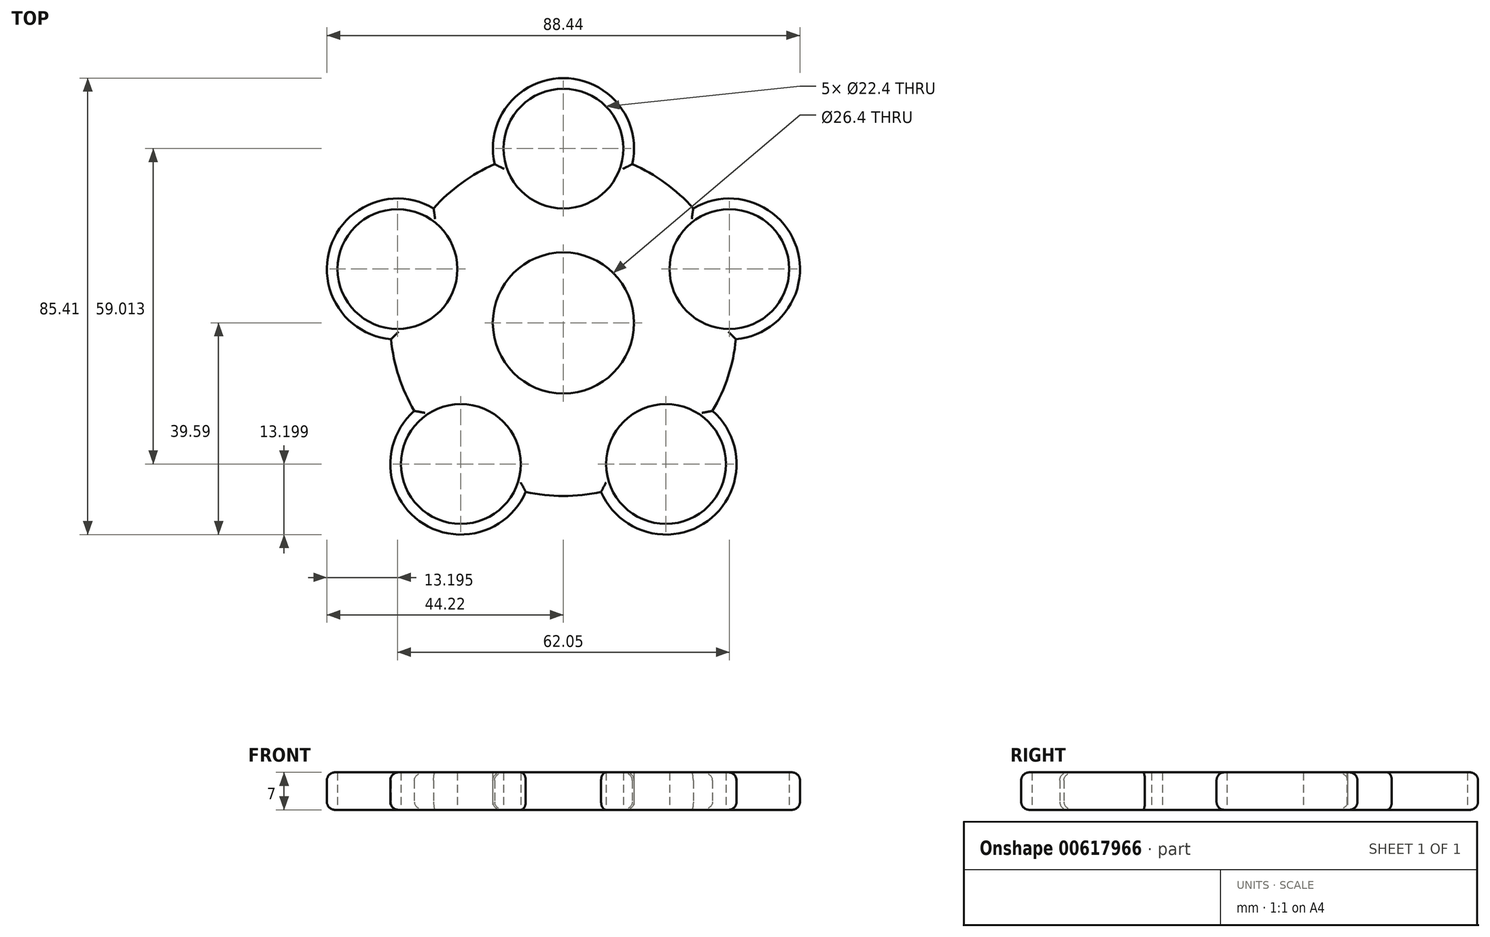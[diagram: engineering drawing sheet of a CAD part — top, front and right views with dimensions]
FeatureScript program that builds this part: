
annotation { "Feature Type Name" : "Feature", "Feature Type Description" : "" }
export const myFeature = defineFeature(function(context is Context, id is Id, definition is map)
    precondition{}
    {
        {
            var Q0;
            Q0=qCreatedBy(makeId("Top.planeOp"),FACE);
            var sketch = newSketch(context, id + "F0", { "sketchPlane" : qUnion([Q0])});
            skCircle(sketch, "E0", {"center": v(0, 0) * mm, "radius": 11.2 * mm});
            skCircle(sketch, "E1", {"center": v(0, 0) * mm, "radius": 13.2 * mm});
            skCircle(sketch, "E2", {"center": v(0, 32.62) * mm, "radius": 11.2 * mm});
            skCircle(sketch, "E3", {"center": v(0, 32.62) * mm, "radius": 13.2 * mm});
            skArc(sketch, "E4.1.0", {"start": v(-24.27, 21.42) * mm, "mid": v(-43.58, 14.16) * mm, "end": v(-32.23, -3.06) * mm});
            skCircle(sketch, "E4.1.1", {"center": v(-31.02, 10.08) * mm, "radius": 11.2 * mm});
            skArc(sketch, "E4.2.0", {"start": v(-27.88, -16.47) * mm, "mid": v(-26.93, -37.07) * mm, "end": v(-7.05, -31.6) * mm});
            skCircle(sketch, "E4.2.1", {"center": v(-19.17, -26.4) * mm, "radius": 11.2 * mm});
            skArc(sketch, "E4.3.0", {"start": v(7.05, -31.6) * mm, "mid": v(26.93, -37.07) * mm, "end": v(27.88, -16.47) * mm});
            skCircle(sketch, "E4.3.1", {"center": v(19.17, -26.4) * mm, "radius": 11.2 * mm});
            skArc(sketch, "E5.1.4.0", {"start": v(32.23, -3.06) * mm, "mid": v(43.58, 14.16) * mm, "end": v(24.27, 21.42) * mm});
            skCircle(sketch, "E5.2.4.0", {"center": v(31.02, 10.08) * mm, "radius": 11.2 * mm});
            skArc(sketch, "E6", {"start": v(25.57, 19.86) * mm, "mid": v(19.03, 26.2) * mm, "end": v(10.99, 30.45) * mm});
            skArc(sketch, "E7.trimOffspring", {"start": v(26.79, -18.18) * mm, "mid": v(30.8, -10) * mm, "end": v(32.36, -1.04) * mm});
            skArc(sketch, "E8.trimOffspring", {"start": v(-9.01, -31.1) * mm, "mid": v(0, -32.38) * mm, "end": v(9.01, -31.1) * mm});
            skArc(sketch, "E9.trimOffspring", {"start": v(-32.36, -1.04) * mm, "mid": v(-30.8, -10) * mm, "end": v(-26.79, -18.18) * mm});
            skArc(sketch, "E10.trimOffspring", {"start": v(-10.99, 30.45) * mm, "mid": v(-19.03, 26.2) * mm, "end": v(-25.57, 19.86) * mm});
            skSolve(sketch);
        }
        {
            var Q0;
            Q0=makeQuery(id+"F0.imprint","IMPRINT",FACE,{"disambiguationData":[TD([[makeQuery(id+"F0.imprint","IMPRINT",EDGE,{"derivedFrom":sQuery(id+"F0.wireOp",EDGE,"E1")}),-1.0]])]});
            var Q1;
            {var subQ0=sQuery(id+"F0.wireOp",EDGE,"E6");var subQ1=sQuery(id+"F0.wireOp",EDGE,"E2");var subQ2=makeQuery(id+"F0.imprint","INTERSECT",VERTEX,{"derivedFrom":[subQ1,subQ0]});Q1=makeQuery(id+"F0.imprint","IMPRINT",FACE,{"disambiguationData":[TD([[makeQuery(id+"F0.imprint","IMPRINT",EDGE,{"disambiguationData":[TD([[subQ2,-1.0]])],"derivedFrom":subQ1}),-1.0]])]});}
            var Q2;
            {var subQ0=sQuery(id+"F0.wireOp",EDGE,"E5.1.4.0");Q2=makeQuery(id+"F0.imprint","IMPRINT",FACE,{"disambiguationData":[TD([[makeQuery(id+"F0.imprint","IMPRINT",EDGE,{"derivedFrom":subQ0}),1.0]])]});}
            var Q3;
            {var subQ0=sQuery(id+"F0.wireOp",EDGE,"E4.3.0");Q3=makeQuery(id+"F0.imprint","IMPRINT",FACE,{"disambiguationData":[TD([[makeQuery(id+"F0.imprint","IMPRINT",EDGE,{"derivedFrom":subQ0}),1.0]])]});}
            var Q4;
            {var subQ0=sQuery(id+"F0.wireOp",EDGE,"E4.2.0");Q4=makeQuery(id+"F0.imprint","IMPRINT",FACE,{"disambiguationData":[TD([[makeQuery(id+"F0.imprint","IMPRINT",EDGE,{"derivedFrom":subQ0}),1.0]])]});}
            var Q5;
            {var subQ0=sQuery(id+"F0.wireOp",EDGE,"E4.1.0");Q5=makeQuery(id+"F0.imprint","IMPRINT",FACE,{"disambiguationData":[TD([[makeQuery(id+"F0.imprint","IMPRINT",EDGE,{"derivedFrom":subQ0}),1.0]])]});}
            var Q6;
            {var subQ0=sQuery(id+"F0.wireOp",EDGE,"E6");var subQ1=sQuery(id+"F0.wireOp",EDGE,"E2");var subQ2=makeQuery(id+"F0.imprint","INTERSECT",VERTEX,{"derivedFrom":[subQ1,subQ0]});Q6=makeQuery(id+"F0.imprint","IMPRINT",FACE,{"disambiguationData":[TD([[makeQuery(id+"F0.imprint","IMPRINT",EDGE,{"disambiguationData":[TD([[subQ2,1.0]])],"derivedFrom":subQ1}),-1.0]])]});}
            extrude(context, id + "F1", {"entities" : qUnion([Q0, Q1, Q2, Q3, Q4, Q5, Q6]), "depth" : 7 * mm, "offsetDistance" : 25 * mm});
        }
        {
            var Q0;
            Q0=makeQuery(id+"F1.opExtrude","CAP_EDGE",EDGE,{"disambiguationData":[OSD([sQuery(id+"F0.wireOp",EDGE,"E10.trimOffspring")])],"isStart":false});
            var Q1;
            Q1=makeQuery(id+"F1.opExtrude","CAP_EDGE",EDGE,{"disambiguationData":[OSD([sQuery(id+"F0.wireOp",EDGE,"E4.1.0")])],"isStart":false});
            var Q2;
            Q2=makeQuery(id+"F1.opExtrude","CAP_EDGE",EDGE,{"disambiguationData":[OSD([sQuery(id+"F0.wireOp",EDGE,"E9.trimOffspring")])],"isStart":false});
            var Q3;
            Q3=makeQuery(id+"F1.opExtrude","CAP_EDGE",EDGE,{"disambiguationData":[OSD([sQuery(id+"F0.wireOp",EDGE,"E4.2.0")])],"isStart":false});
            var Q4;
            Q4=makeQuery(id+"F1.opExtrude","CAP_EDGE",EDGE,{"disambiguationData":[OSD([sQuery(id+"F0.wireOp",EDGE,"E8.trimOffspring")])],"isStart":false});
            var Q5;
            Q5=makeQuery(id+"F1.opExtrude","CAP_EDGE",EDGE,{"disambiguationData":[OSD([sQuery(id+"F0.wireOp",EDGE,"E4.3.0")])],"isStart":false});
            var Q6;
            Q6=makeQuery(id+"F1.opExtrude","CAP_EDGE",EDGE,{"disambiguationData":[OSD([sQuery(id+"F0.wireOp",EDGE,"E7.trimOffspring")])],"isStart":false});
            var Q7;
            Q7=makeQuery(id+"F1.opExtrude","CAP_EDGE",EDGE,{"disambiguationData":[OSD([sQuery(id+"F0.wireOp",EDGE,"E5.1.4.0")])],"isStart":false});
            var Q8;
            Q8=makeQuery(id+"F1.opExtrude","CAP_EDGE",EDGE,{"disambiguationData":[OSD([sQuery(id+"F0.wireOp",EDGE,"E6")])],"isStart":false});
            var Q9;
            Q9=makeQuery(id+"F1.opExtrude","CAP_EDGE",EDGE,{"disambiguationData":[OSD([sQuery(id+"F0.wireOp",EDGE,"E3")])],"isStart":false});
            fillet(context, id + "F2", {"entities" : qUnion([Q0, Q1, Q2, Q3, Q4, Q5, Q6, Q7, Q8, Q9]), "radius" : 1.5 * mm, "tangentPropagation" : true, "allowEdgeOverflow" : false});
        }
        {
            var Q0;
            Q0=makeQuery(id+"F1.opExtrude","CAP_EDGE",EDGE,{"disambiguationData":[OSD([sQuery(id+"F0.wireOp",EDGE,"E4.2.0")])],"isStart":true});
            var Q1;
            Q1=makeQuery(id+"F1.opExtrude","CAP_EDGE",EDGE,{"disambiguationData":[OSD([sQuery(id+"F0.wireOp",EDGE,"E4.3.0")])],"isStart":true});
            var Q2;
            Q2=makeQuery(id+"F1.opExtrude","CAP_EDGE",EDGE,{"disambiguationData":[OSD([sQuery(id+"F0.wireOp",EDGE,"E5.1.4.0")])],"isStart":true});
            var Q3;
            Q3=makeQuery(id+"F1.opExtrude","CAP_EDGE",EDGE,{"disambiguationData":[OSD([sQuery(id+"F0.wireOp",EDGE,"E3")])],"isStart":true});
            var Q4;
            Q4=makeQuery(id+"F1.opExtrude","CAP_EDGE",EDGE,{"disambiguationData":[OSD([sQuery(id+"F0.wireOp",EDGE,"E4.1.0")])],"isStart":true});
            var Q5;
            Q5=makeQuery(id+"F1.opExtrude","CAP_EDGE",EDGE,{"disambiguationData":[OSD([sQuery(id+"F0.wireOp",EDGE,"E10.trimOffspring")])],"isStart":true});
            var Q6;
            Q6=makeQuery(id+"F1.opExtrude","CAP_EDGE",EDGE,{"disambiguationData":[OSD([sQuery(id+"F0.wireOp",EDGE,"E6")])],"isStart":true});
            var Q7;
            Q7=makeQuery(id+"F1.opExtrude","CAP_EDGE",EDGE,{"disambiguationData":[OSD([sQuery(id+"F0.wireOp",EDGE,"E7.trimOffspring")])],"isStart":true});
            var Q8;
            Q8=makeQuery(id+"F1.opExtrude","CAP_EDGE",EDGE,{"disambiguationData":[OSD([sQuery(id+"F0.wireOp",EDGE,"E8.trimOffspring")])],"isStart":true});
            var Q9;
            Q9=makeQuery(id+"F1.opExtrude","CAP_EDGE",EDGE,{"disambiguationData":[OSD([sQuery(id+"F0.wireOp",EDGE,"E9.trimOffspring")])],"isStart":true});
            fillet(context, id + "F3", {"entities" : qUnion([Q0, Q1, Q2, Q3, Q4, Q5, Q6, Q7, Q8, Q9]), "radius" : 1.5 * mm, "tangentPropagation" : true, "allowEdgeOverflow" : false});
        }
    });
